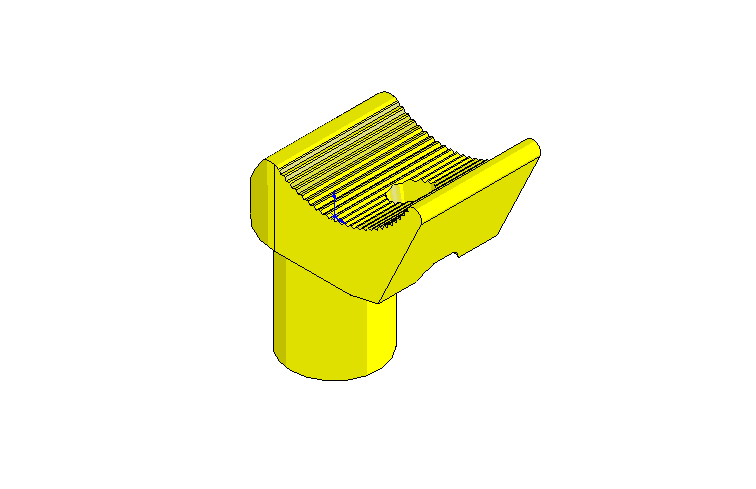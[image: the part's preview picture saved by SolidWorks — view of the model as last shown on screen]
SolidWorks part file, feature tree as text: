
SOLIDWORKS PART (.sldprt)
format: sldprt  version: not decoded by parser v0  size: 493,056 bytes
history: native  units: mm
features: sketch x6, cut_extrude x4, plane x3, extrude x2, material x1, pattern_circular x1 (+10 scaffold rows collapsed)
feature tree (27):
  scaffold x10  (default folders/planes/origin — collapsed)
  material  "Matériau <non spécifié>"
  plane  "Plan de face"
  plane  "Plan de dessus"
  plane  "Plan de droite"
  sketch  "Esquisse1"  dims[D1=22.0mm]
  extrude  "Extrusion1"  Depth=28mm
  sketch  "Esquisse3"  dims[D1=30.0mm D2=52.0mm]
  extrude  "Extrusion2"  Depth=27mm
  sketch  "Esquisse4"  dims[c1.D1=3.5mm c1.D2=2.0mm c1.D3=1.0mm c1.D5=22.5mm c1.D7=3.5mm c1.D4=14.0mm c1.D6=38.0mm c2.D7=2.0mm c2.D8=19.0mm c2.D9=26.0mm c2.D10=2.0mm c2.D11=1.0mm c2.D6=2.0mm c3.D7=19.0mm c3.D12=~7.070368mm c3.D3=19.0mm c3.D8=26.0mm c3.D9=1.5mm]
  cut_extrude  "Enlèv. mat.-Extru.2"  [1 undecoded]
  sketch  "Esquisse5"  dims[c1.D2=22.5mm c1.D1=1.0mm c2.D2=~22.994444mm c2.D1=23.0mm c3.D2=1.2mm c3.D3=~29.249793mm c4.D3=60.0deg]
  cut_extrude  "Enlèv. mat.-Extru.3"  [1 undecoded]
  pattern_circular  "Répétition circulaire1"  Count=24 Angle=4deg
  sketch  "Esquisse6"  dims[D1=9.0mm D2=22.0mm]
  cut_extrude  "Enlèv. mat.-Extru.4"  [1 undecoded]
  sketch  "Esquisse7"  dims[D1=13.0mm]
  cut_extrude  "Enlèv. mat.-Extru.5"  Depth=3mm
decode coverage: 10 of 13 modeling features carry decoded parameters
note: ~ marks probable driven/reference dimensions
note: 3 parameter values undecoded
summary: no parameter record found for 3 features
note: suppression state not decoded; provenance and decode notes live in map.json
